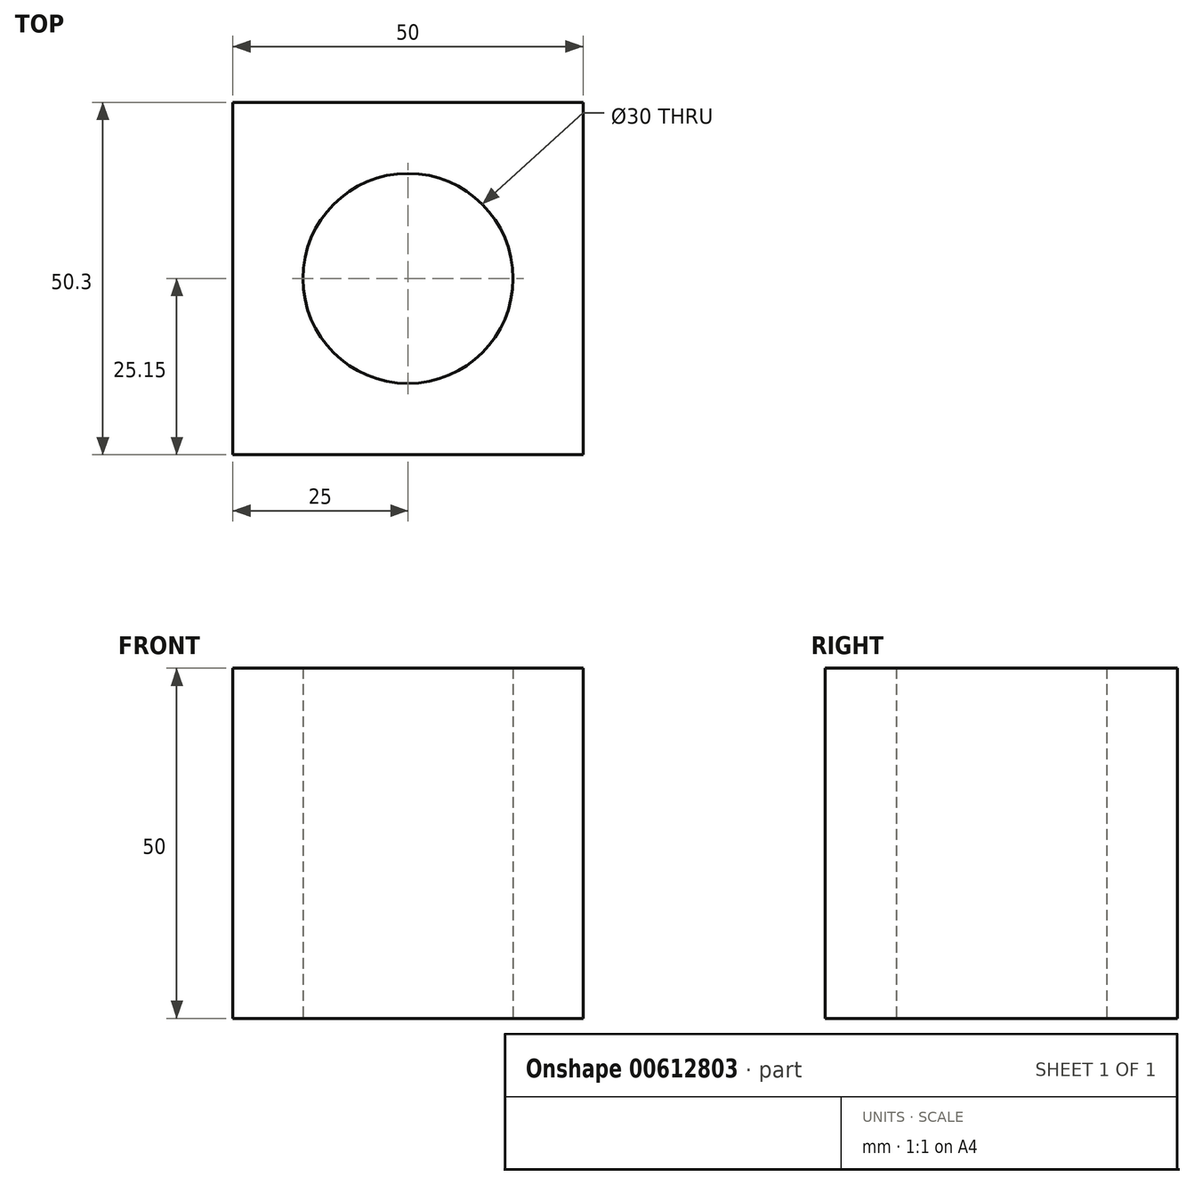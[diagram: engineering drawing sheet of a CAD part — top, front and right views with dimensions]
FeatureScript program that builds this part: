
annotation { "Feature Type Name" : "Feature", "Feature Type Description" : "" }
export const myFeature = defineFeature(function(context is Context, id is Id, definition is map)
    precondition{}
    {
        {
            var Q0;
            Q0=qCreatedBy(makeId("Top.planeOp"),FACE);
            var sketch = newSketch(context, id + "F0", { "sketchPlane" : qUnion([Q0])});
            skLineSegment(sketch, "E0.bottom", {"start": v(-25, 25.15) * mm, "end": v(25, 25.15) * mm});
            skLineSegment(sketch, "E0.top", {"start": v(-25, -25.15) * mm, "end": v(25, -25.15) * mm});
            skLineSegment(sketch, "E0.left", {"start": v(-25, 25.15) * mm, "end": v(-25, -25.15) * mm});
            skLineSegment(sketch, "E0.right", {"start": v(25, 25.15) * mm, "end": v(25, -25.15) * mm});
            skPoint(sketch, "E0.middle", {"position": v(0, 0) * mm});
            skCircle(sketch, "E1", {"center": v(0, 0) * mm, "radius": 15 * mm});
            skSolve(sketch);
        }
        {
            var Q0;
            Q0 = qSketchRegion(id + "F0", true);
            extrude(context, id + "F1", {"entities" : qUnion([Q0]), "depth" : 50 * mm, "offsetDistance" : 25 * mm});
        }
    });
